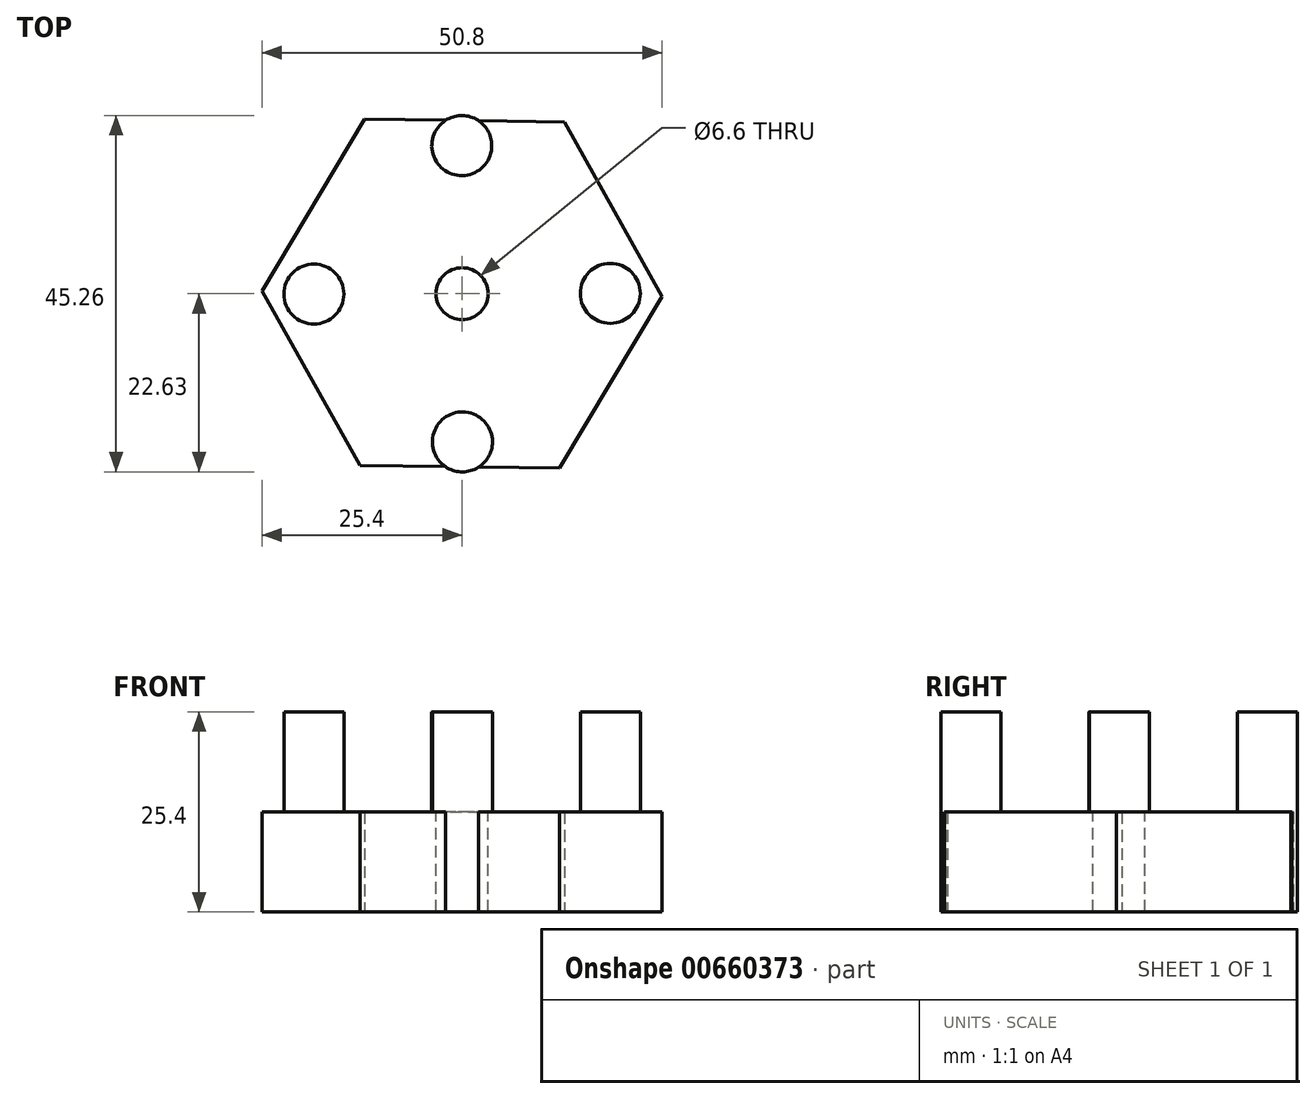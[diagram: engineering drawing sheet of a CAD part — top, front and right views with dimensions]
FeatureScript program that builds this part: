
annotation { "Feature Type Name" : "Feature", "Feature Type Description" : "" }
export const myFeature = defineFeature(function(context is Context, id is Id, definition is map)
    precondition{}
    {
        {
            var Q0;
            Q0=qCreatedBy(makeId("Top.planeOp"),FACE);
            var sketch = newSketch(context, id + "F0", { "sketchPlane" : qUnion([Q0])});
            skCircle(sketch, "E0.cCircle", {"center": v(0, 0) * mm, "radius": 25.4 * mm, "construction": true});
            skLineSegment(sketch, "E0.0", {"start": v(12.4, -22.17) * mm, "end": v(-13, -21.83) * mm});
            skLineSegment(sketch, "E0.1", {"start": v(-13, -21.83) * mm, "end": v(-25.4, 0.34) * mm});
            skLineSegment(sketch, "E0.2", {"start": v(-25.4, 0.34) * mm, "end": v(-12.4, 22.17) * mm});
            skLineSegment(sketch, "E0.3", {"start": v(-12.4, 22.17) * mm, "end": v(13, 21.83) * mm});
            skLineSegment(sketch, "E0.4", {"start": v(13, 21.83) * mm, "end": v(25.4, -0.34) * mm});
            skLineSegment(sketch, "E0.5", {"start": v(25.4, -0.34) * mm, "end": v(12.4, -22.17) * mm});
            skLineSegment(sketch, "E1", {"start": v(0, 22) * mm, "end": v(-0.04, 18.82) * mm, "construction": true});
            skCircle(sketch, "E2", {"center": v(-0.04, 18.82) * mm, "radius": 3.81 * mm});
            skCircle(sketch, "E3.1.0", {"center": v(-18.82, -0.04) * mm, "radius": 3.81 * mm});
            skCircle(sketch, "E3.2.0", {"center": v(0.04, -18.82) * mm, "radius": 3.81 * mm});
            skCircle(sketch, "E4.1.3.0", {"center": v(18.82, 0.04) * mm, "radius": 3.81 * mm});
            skSolve(sketch);
        }
        {
            var Q0;
            Q0 = qSketchRegion(id + "F0", true);
            extrude(context, id + "F1", {"entities" : qUnion([Q0]), "depth" : 12.7 * mm, "offsetDistance" : 25.4 * mm});
        }
        {
            var Q0;
            Q0=makeQuery(id+"F1.opExtrude","CAP_FACE",FACE,{"disambiguationData":[OSD([sQuery(id+"F0.wireOp",EDGE,"E0.0"),sQuery(id+"F0.wireOp",EDGE,"E0.1"),sQuery(id+"F0.wireOp",EDGE,"E0.2"),sQuery(id+"F0.wireOp",EDGE,"E0.3"),sQuery(id+"F0.wireOp",EDGE,"E0.4"),sQuery(id+"F0.wireOp",EDGE,"E0.5")])],"isStart":false});
            var sketch = newSketch(context, id + "F2", { "sketchPlane" : qUnion([Q0])});
            skCircle(sketch, "E5", {"center": v(0, 0) * mm, "radius": 3.3 * mm});
            skSolve(sketch);
        }
        {
            var Q0;
            Q0 = qSketchRegion(id + "F2", true);
            extrude(context, id + "F3", {"entities" : qUnion([Q0]), "operationType" : NewBodyOperationType.REMOVE, "oppositeDirection" : true, "depth" : 25.4 * mm, "offsetDistance" : 25.4 * mm});
        }
        {
            var Q0;
            Q0=makeQuery(id+"F0.imprint","IMPRINT",FACE,{"disambiguationData":[TD([[makeQuery(id+"F0.imprint","IMPRINT",EDGE,{"derivedFrom":sQuery(id+"F0.wireOp",EDGE,"E2")}),1.0]])]});
            var Q1;
            Q1=makeQuery(id+"F0.imprint","IMPRINT",FACE,{"disambiguationData":[TD([[makeQuery(id+"F0.imprint","IMPRINT",EDGE,{"derivedFrom":sQuery(id+"F0.wireOp",EDGE,"E4.1.7.0")}),1.0]])]});
            var Q2;
            Q2=makeQuery(id+"F0.imprint","IMPRINT",FACE,{"disambiguationData":[TD([[makeQuery(id+"F0.imprint","IMPRINT",EDGE,{"derivedFrom":sQuery(id+"F0.wireOp",EDGE,"E4.1.5.0")}),1.0]])]});
            var Q3;
            Q3=makeQuery(id+"F0.imprint","IMPRINT",FACE,{"disambiguationData":[TD([[makeQuery(id+"F0.imprint","IMPRINT",EDGE,{"derivedFrom":sQuery(id+"F0.wireOp",EDGE,"E4.1.4.0")}),1.0]])]});
            var Q4;
            Q4=makeQuery(id+"F0.imprint","IMPRINT",FACE,{"disambiguationData":[TD([[makeQuery(id+"F0.imprint","IMPRINT",EDGE,{"derivedFrom":sQuery(id+"F0.wireOp",EDGE,"E4.1.6.0")}),1.0]])]});
            var Q5;
            Q5=makeQuery(id+"F0.imprint","IMPRINT",FACE,{"disambiguationData":[TD([[makeQuery(id+"F0.imprint","IMPRINT",EDGE,{"derivedFrom":sQuery(id+"F0.wireOp",EDGE,"E4.1.3.0")}),1.0]])]});
            var Q6;
            Q6=makeQuery(id+"F0.imprint","IMPRINT",FACE,{"disambiguationData":[TD([[makeQuery(id+"F0.imprint","IMPRINT",EDGE,{"derivedFrom":sQuery(id+"F0.wireOp",EDGE,"E3.2.0")}),1.0]])]});
            var Q7;
            Q7=makeQuery(id+"F0.imprint","IMPRINT",FACE,{"disambiguationData":[TD([[makeQuery(id+"F0.imprint","IMPRINT",EDGE,{"derivedFrom":sQuery(id+"F0.wireOp",EDGE,"E3.1.0")}),1.0]])]});
            extrude(context, id + "F4", {"entities" : qUnion([Q0, Q1, Q2, Q3, Q4, Q5, Q6, Q7]), "operationType" : NewBodyOperationType.ADD, "depth" : 25.4 * mm, "offsetDistance" : 25.4 * mm});
        }
    });
